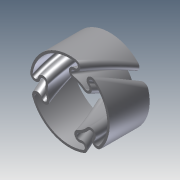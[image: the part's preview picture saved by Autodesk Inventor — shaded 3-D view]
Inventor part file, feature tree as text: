
AUTODESK INVENTOR PART (.ipt)
format: ipt  version: 2012 (Build 160160000, 160)  size: 583,680 bytes
history: native  units: in
note: dims shown in document units (in); Inventor stores cm internally (conversion verified against a paired STEP export)
features: extrude x2, sketch x2, mirror x1, pattern_circular x1, helix x1
ambient origin geometry x8: Origin, YZ Plane, XZ Plane, XY Plane, X Axis, Y Axis, Z Axis, Center Point
bodies: Solid1 (feature_tree)
feature tree (7):
  extrude  "Extrusion1"  Depth=0.275in
  mirror  "Mirror1"
  pattern_circular  "Circular Pattern1"  Angle=60.0deg  [1 undecoded]
  sketch  "Sketch3"  dims[d6=45.0deg d7=60.0deg d8=0.0295in d9=0.5in d10=0.0in d11=1.1811in d12=360.0deg d14=0.0in d15=0.0in d16=0.5in d17=0.5in d18=0.0394in d19=0.0in d20=90.0deg d21=90.0deg d22=0.0in d23=0.0in]
  extrude  "Extrusion2"  Depth=0.0295in
  helix  "Coil1"  [1 undecoded]
  sketch  "Sketch2"  dims[d4=0.5in d5=0.275in]
note: 2 required parameter values undecoded (feature->parameter linkage not recoverable at this tier; creation-order binding heuristic only, values carry confidence <= 0.55)
